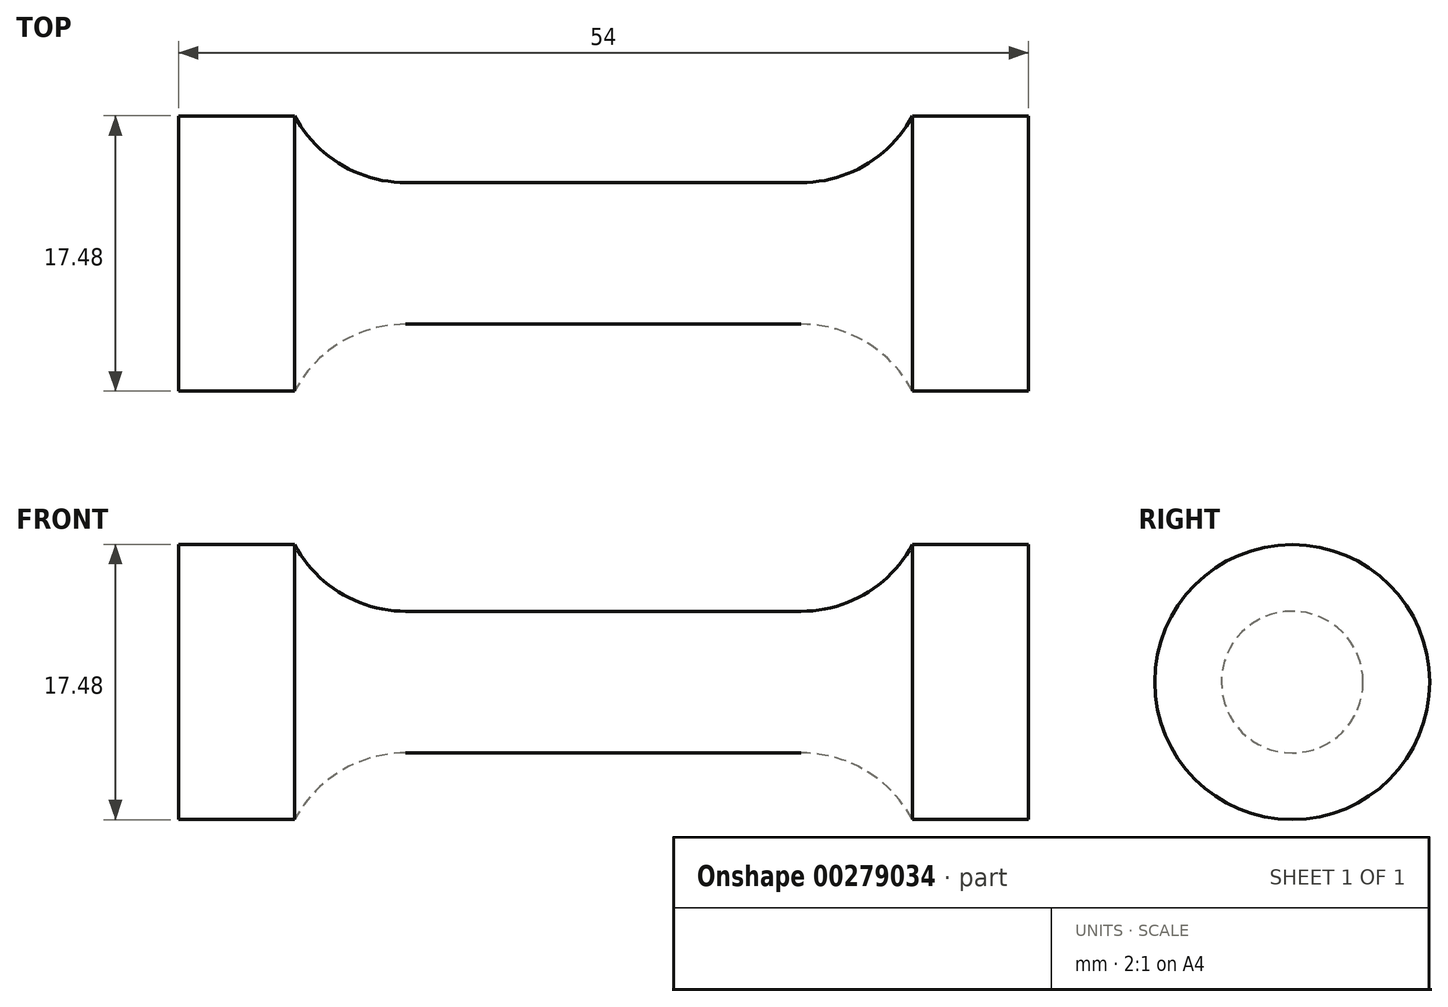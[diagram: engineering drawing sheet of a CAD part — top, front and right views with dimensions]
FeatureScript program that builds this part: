
annotation { "Feature Type Name" : "Feature", "Feature Type Description" : "" }
export const myFeature = defineFeature(function(context is Context, id is Id, definition is map)
    precondition{}
    {
        {
            var Q0;
            Q0=qCreatedBy(makeId("Front.planeOp"),FACE);
            var sketch = newSketch(context, id + "F0", { "sketchPlane" : qUnion([Q0])});
            skLineSegment(sketch, "E0", {"start": v(0, 4.5) * mm, "end": v(12.56, 4.5) * mm});
            skArc(sketch, "E1", {"start": v(12.56, 4.5) * mm, "mid": v(16.67, 5.64) * mm, "end": v(19.62, 8.74) * mm});
            skLineSegment(sketch, "E2", {"start": v(19.62, 8.74) * mm, "end": v(27, 8.74) * mm});
            skLineSegment(sketch, "E3", {"start": v(27, 8.74) * mm, "end": v(27, 0) * mm});
            skLineSegment(sketch, "E4.MirrorCS", {"start": v(0, 4.5) * mm, "end": v(-12.56, 4.5) * mm});
            skLineSegment(sketch, "E5.MirrorCS", {"start": v(-27, 8.74) * mm, "end": v(-27, 0) * mm});
            skLineSegment(sketch, "E6.MirrorCS", {"start": v(-19.62, 8.74) * mm, "end": v(-27, 8.74) * mm});
            skArc(sketch, "E7.MirrorCS", {"start": v(-12.56, 4.5) * mm, "mid": v(-16.67, 5.64) * mm, "end": v(-19.62, 8.74) * mm});
            skLineSegment(sketch, "E8", {"start": v(-27, 0) * mm, "end": v(27, 0) * mm});
            skSolve(sketch);
        }
        {
            var Q0;
            Q0=makeQuery(id+"F0.imprint","IMPRINT",FACE,{"disambiguationData":[TD([[makeQuery(id+"F0.imprint","IMPRINT",EDGE,{"derivedFrom":sQuery(id+"F0.wireOp",EDGE,"E0")}),-1.0]])]});
            var Q1;
            Q1=sQuery(id+"F0.wireOp",EDGE,"E8");
            revolve(context, id + "F1", {"entities" : qUnion([Q0]), "axis" : qUnion([Q1]), "revolveType" : RevolveType.FULL});
        }
    });
